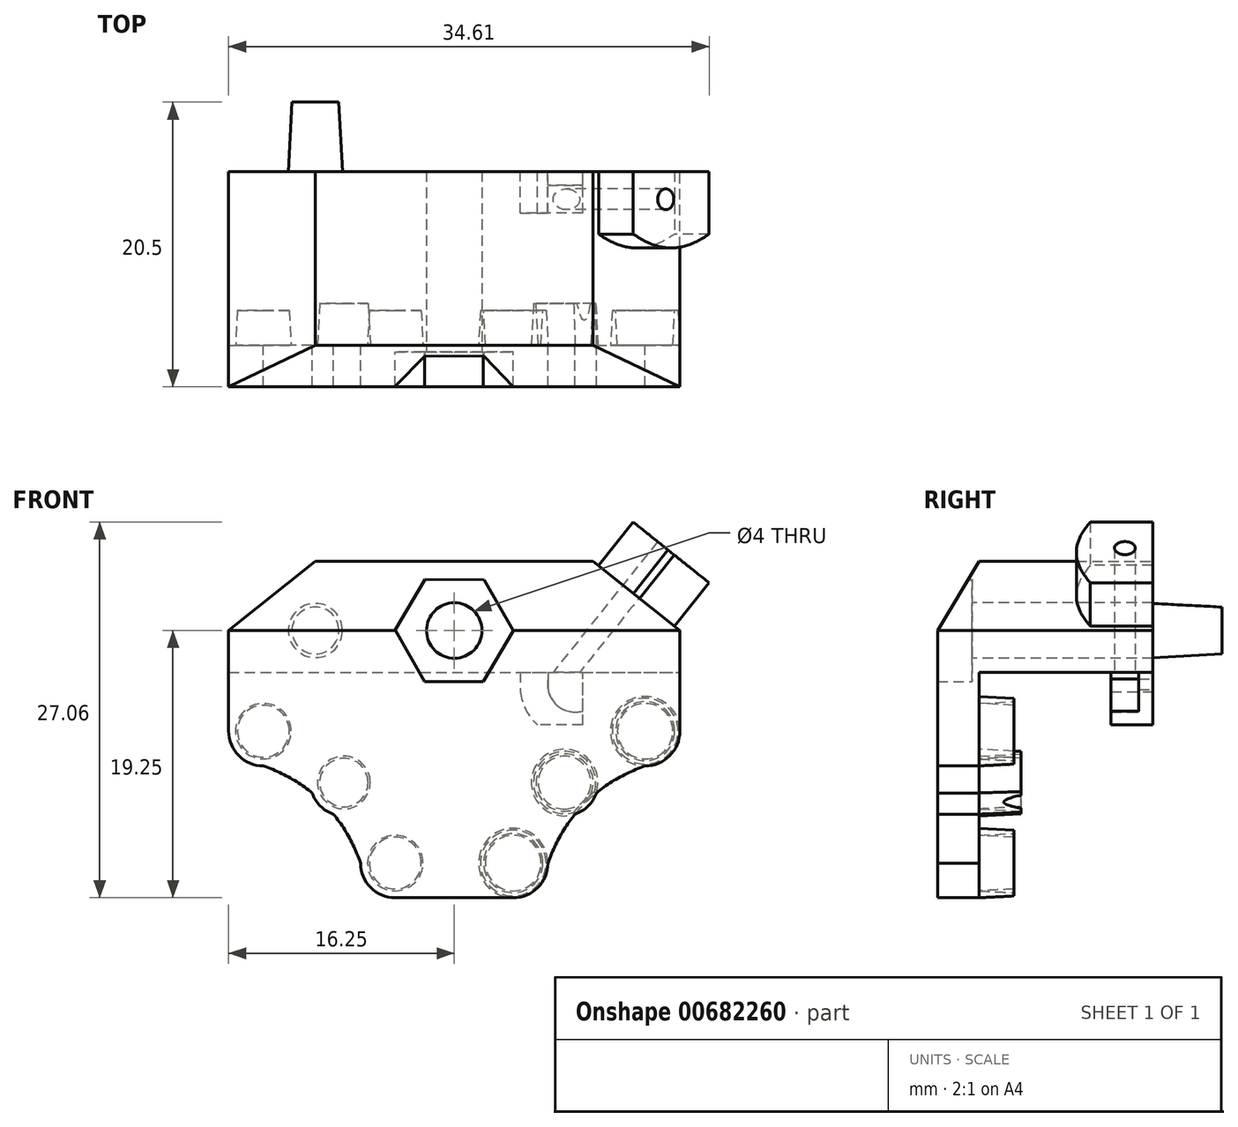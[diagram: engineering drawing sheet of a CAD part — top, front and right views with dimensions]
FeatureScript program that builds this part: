
annotation { "Feature Type Name" : "Feature", "Feature Type Description" : "" }
export const myFeature = defineFeature(function(context is Context, id is Id, definition is map)
    precondition{}
    {
        {
            var Q0;
            Q0=qCreatedBy(makeId("Front.planeOp"),FACE);
            var sketch = newSketch(context, id + "F0", { "sketchPlane" : qUnion([Q0])});
            skLineSegment(sketch, "E0", {"start": v(0, 0) * mm, "end": v(-4.25, 0) * mm});
            skLineSegment(sketch, "E1", {"start": v(0, 0) * mm, "end": v(0, -4.25) * mm});
            skLineSegment(sketch, "E2", {"start": v(0, 0) * mm, "end": v(0, -7.95) * mm});
            skLineSegment(sketch, "E3", {"start": v(0, 0) * mm, "end": v(-7.95, 0) * mm});
            skLineSegment(sketch, "E4", {"start": v(0, 0) * mm, "end": v(0, -13.75) * mm});
            skLineSegment(sketch, "E5", {"start": v(0, 0) * mm, "end": v(-13.75, 0) * mm});
            skCircle(sketch, "E6", {"center": v(-4.25, -13.75) * mm, "radius": 2 * mm});
            skCircle(sketch, "E7", {"center": v(-13.75, -4.25) * mm, "radius": 2 * mm});
            skCircle(sketch, "E8", {"center": v(-7.95, -7.95) * mm, "radius": 1.9 * mm});
            skLineSegment(sketch, "E9", {"start": v(0, 0) * mm, "end": v(0, 3) * mm});
            skCircle(sketch, "E10", {"center": v(0, 3) * mm, "radius": 2 * mm});
            skCircle(sketch, "E11.cCircle", {"center": v(0, 3) * mm, "radius": 4.25 * mm, "construction": true});
            skLineSegment(sketch, "E11.0", {"start": v(2.15, 6.67) * mm, "end": v(4.25, 2.97) * mm});
            skLineSegment(sketch, "E11.1", {"start": v(4.25, 2.97) * mm, "end": v(2.1, -0.7) * mm});
            skLineSegment(sketch, "E11.2", {"start": v(2.1, -0.7) * mm, "end": v(-2.15, -0.67) * mm});
            skLineSegment(sketch, "E11.3", {"start": v(-2.15, -0.67) * mm, "end": v(-4.25, 3.03) * mm});
            skLineSegment(sketch, "E11.4", {"start": v(-4.25, 3.03) * mm, "end": v(-2.1, 6.7) * mm});
            skLineSegment(sketch, "E11.5", {"start": v(-2.1, 6.7) * mm, "end": v(2.15, 6.67) * mm});
            skCircle(sketch, "E12.MirrorC", {"center": v(4.25, -13.75) * mm, "radius": 2 * mm});
            skCircle(sketch, "E13.MirrorC", {"center": v(7.95, -7.95) * mm, "radius": 1.9 * mm});
            skCircle(sketch, "E14.MirrorC", {"center": v(13.75, -4.25) * mm, "radius": 2 * mm});
            skLineSegment(sketch, "E15", {"start": v(0, 0) * mm, "end": v(0, 12) * mm});
            skCircle(sketch, "E16", {"center": v(-13.75, -4.25) * mm, "radius": 2.5 * mm});
            skCircle(sketch, "E17", {"center": v(-7.95, -7.95) * mm, "radius": 2.4 * mm});
            skCircle(sketch, "E18", {"center": v(-4.25, -13.75) * mm, "radius": 2.5 * mm});
            skLineSegment(sketch, "E19", {"start": v(-4.25, -16.25) * mm, "end": v(0, -16.25) * mm});
            skLineSegment(sketch, "E20", {"start": v(-16.25, -4.25) * mm, "end": v(-16.25, 0) * mm});
            skLineSegment(sketch, "E21", {"start": v(-16.25, 0) * mm, "end": v(-16.25, 3) * mm});
            skLineSegment(sketch, "E22", {"start": v(-16.25, 3) * mm, "end": v(-10, 8) * mm});
            skLineSegment(sketch, "E23", {"start": v(-10, 8) * mm, "end": v(0, 8) * mm});
            skLineSegment(sketch, "E24.MirrorCS", {"start": v(10, 8) * mm, "end": v(0, 8) * mm});
            skLineSegment(sketch, "E25.MirrorCS", {"start": v(16.25, 3) * mm, "end": v(10, 8) * mm});
            skLineSegment(sketch, "E26.MirrorCS", {"start": v(16.25, 0) * mm, "end": v(16.25, 3) * mm});
            skLineSegment(sketch, "E27.MirrorCS", {"start": v(16.25, -4.25) * mm, "end": v(16.25, 0) * mm});
            skCircle(sketch, "E28.MirrorC", {"center": v(13.75, -4.25) * mm, "radius": 2.5 * mm});
            skCircle(sketch, "E29.MirrorC", {"center": v(4.25, -13.75) * mm, "radius": 2.5 * mm});
            skLineSegment(sketch, "E30.MirrorCS", {"start": v(4.25, -16.25) * mm, "end": v(0, -16.25) * mm});
            skFitSpline(sketch, "E31", {"points": [v(-6.75, -13.75) * mm, v(-13.75, -6.75) * mm], "startDerivative": vector(-3.6, 10.2) * mm, "endDerivative": vector(-10.2, 3.6) * mm});
            skFitSpline(sketch, "E32.MirrorCS", {"points": [v(6.75, -13.75) * mm, v(13.75, -6.75) * mm], "startDerivative": vector(3.6, 10.2) * mm, "endDerivative": vector(10.2, 3.6) * mm});
            skCircle(sketch, "E33.MirrorC", {"center": v(7.95, -7.95) * mm, "radius": 2.4 * mm});
            skLineSegment(sketch, "E34", {"start": v(-16.25, 0) * mm, "end": v(16.25, 0) * mm});
            skSolve(sketch);
        }
        {
            var Q0;
            {var subQ7=sQuery(id+"F0.wireOp",EDGE,"E11.4");Q0=makeQuery(id+"F0.imprint","IMPRINT",FACE,{"disambiguationData":[TD([[makeQuery(id+"F0.imprint","IMPRINT",EDGE,{"derivedFrom":subQ7}),1.0]])]});}
            var Q1;
            {var subQ4=sQuery(id+"F0.wireOp",EDGE,"E11.0");Q1=makeQuery(id+"F0.imprint","IMPRINT",FACE,{"disambiguationData":[TD([[makeQuery(id+"F0.imprint","IMPRINT",EDGE,{"derivedFrom":subQ4}),1.0]])]});}
            var Q2;
            {var subQ31=sQuery(id+"F0.wireOp",EDGE,"E19");Q2=makeQuery(id+"F0.imprint","IMPRINT",FACE,{"disambiguationData":[TD([[makeQuery(id+"F0.imprint","IMPRINT",EDGE,{"derivedFrom":subQ31}),1.0]])]});}
            var Q3;
            {var subQ0=sQuery(id+"F0.wireOp",EDGE,"E31");var subQ1=sQuery(id+"F0.wireOp",EDGE,"E17");var subQ2=makeQuery(id+"F0.imprint","INTERSECT",VERTEX,{"disambiguationData":[OD(0.0)],"derivedFrom":[subQ1,subQ0]});Q3=makeQuery(id+"F0.imprint","IMPRINT",FACE,{"disambiguationData":[TD([[makeQuery(id+"F0.imprint","IMPRINT",EDGE,{"disambiguationData":[TD([[subQ2,1.0]])],"derivedFrom":subQ1}),1.0]])]});}
            var Q4;
            Q4=makeQuery(id+"F0.imprint","IMPRINT",FACE,{"disambiguationData":[TD([[makeQuery(id+"F0.imprint","IMPRINT",EDGE,{"derivedFrom":sQuery(id+"F0.wireOp",EDGE,"E8")}),-1.0]])]});
            var Q5;
            Q5=makeQuery(id+"F0.imprint","IMPRINT",FACE,{"disambiguationData":[TD([[makeQuery(id+"F0.imprint","IMPRINT",EDGE,{"derivedFrom":sQuery(id+"F0.wireOp",EDGE,"E8")}),1.0]])]});
            var Q6;
            Q6=makeQuery(id+"F0.imprint","IMPRINT",FACE,{"disambiguationData":[TD([[makeQuery(id+"F0.imprint","IMPRINT",EDGE,{"derivedFrom":sQuery(id+"F0.wireOp",EDGE,"E7")}),-1.0]])]});
            var Q7;
            Q7=makeQuery(id+"F0.imprint","IMPRINT",FACE,{"disambiguationData":[TD([[makeQuery(id+"F0.imprint","IMPRINT",EDGE,{"derivedFrom":sQuery(id+"F0.wireOp",EDGE,"E7")}),1.0]])]});
            var Q8;
            Q8=makeQuery(id+"F0.imprint","IMPRINT",FACE,{"disambiguationData":[TD([[makeQuery(id+"F0.imprint","IMPRINT",EDGE,{"derivedFrom":sQuery(id+"F0.wireOp",EDGE,"E6")}),1.0]])]});
            var Q9;
            Q9=makeQuery(id+"F0.imprint","IMPRINT",FACE,{"disambiguationData":[TD([[makeQuery(id+"F0.imprint","IMPRINT",EDGE,{"derivedFrom":sQuery(id+"F0.wireOp",EDGE,"E6")}),-1.0]])]});
            var Q10;
            Q10=makeQuery(id+"F0.imprint","IMPRINT",FACE,{"disambiguationData":[TD([[makeQuery(id+"F0.imprint","IMPRINT",EDGE,{"derivedFrom":sQuery(id+"F0.wireOp",EDGE,"E12.MirrorC")}),-1.0]])]});
            var Q11;
            Q11=makeQuery(id+"F0.imprint","IMPRINT",FACE,{"disambiguationData":[TD([[makeQuery(id+"F0.imprint","IMPRINT",EDGE,{"derivedFrom":sQuery(id+"F0.wireOp",EDGE,"E12.MirrorC")}),1.0]])]});
            var Q12;
            {var subQ0=sQuery(id+"F0.wireOp",EDGE,"E33.MirrorC");var subQ1=sQuery(id+"F0.wireOp",EDGE,"E32.MirrorCS");var subQ2=makeQuery(id+"F0.imprint","INTERSECT",VERTEX,{"disambiguationData":[OD(0.0)],"derivedFrom":[subQ1,subQ0]});Q12=makeQuery(id+"F0.imprint","IMPRINT",FACE,{"disambiguationData":[TD([[makeQuery(id+"F0.imprint","IMPRINT",EDGE,{"disambiguationData":[TD([[subQ2,-1.0]])],"derivedFrom":subQ1}),-1.0]])]});}
            var Q13;
            Q13=makeQuery(id+"F0.imprint","IMPRINT",FACE,{"disambiguationData":[TD([[makeQuery(id+"F0.imprint","IMPRINT",EDGE,{"derivedFrom":sQuery(id+"F0.wireOp",EDGE,"E13.MirrorC")}),1.0]])]});
            var Q14;
            Q14=makeQuery(id+"F0.imprint","IMPRINT",FACE,{"disambiguationData":[TD([[makeQuery(id+"F0.imprint","IMPRINT",EDGE,{"derivedFrom":sQuery(id+"F0.wireOp",EDGE,"E13.MirrorC")}),-1.0]])]});
            var Q15;
            Q15=makeQuery(id+"F0.imprint","IMPRINT",FACE,{"disambiguationData":[TD([[makeQuery(id+"F0.imprint","IMPRINT",EDGE,{"derivedFrom":sQuery(id+"F0.wireOp",EDGE,"E14.MirrorC")}),1.0]])]});
            var Q16;
            Q16=makeQuery(id+"F0.imprint","IMPRINT",FACE,{"disambiguationData":[TD([[makeQuery(id+"F0.imprint","IMPRINT",EDGE,{"derivedFrom":sQuery(id+"F0.wireOp",EDGE,"E14.MirrorC")}),-1.0]])]});
            extrude(context, id + "F1", {"entities" : qUnion([Q0, Q1, Q2, Q3, Q4, Q5, Q6, Q7, Q8, Q9, Q10, Q11, Q12, Q13, Q14, Q15, Q16]), "depth" : 3 * mm, "offsetDistance" : 25 * mm});
        }
        {
            var Q0;
            Q0=makeQuery(id+"F0.imprint","IMPRINT",FACE,{"disambiguationData":[TD([[makeQuery(id+"F0.imprint","IMPRINT",EDGE,{"derivedFrom":sQuery(id+"F0.wireOp",EDGE,"E8")}),1.0]])]});
            var Q1;
            Q1=makeQuery(id+"F0.imprint","IMPRINT",FACE,{"disambiguationData":[TD([[makeQuery(id+"F0.imprint","IMPRINT",EDGE,{"derivedFrom":sQuery(id+"F0.wireOp",EDGE,"E13.MirrorC")}),-1.0]])]});
            extrude(context, id + "F2", {"entities" : qUnion([Q0, Q1]), "operationType" : NewBodyOperationType.ADD, "oppositeDirection" : true, "depth" : 3 * mm, "offsetDistance" : 25 * mm, "hasDraft" : true, "draftAngle" : 3 * degree, "draftPullDirection" : true});
        }
        {
            var Q0;
            {var subQ7=sQuery(id+"F0.wireOp",EDGE,"E11.4");Q0=makeQuery(id+"F0.imprint","IMPRINT",FACE,{"disambiguationData":[TD([[makeQuery(id+"F0.imprint","IMPRINT",EDGE,{"derivedFrom":subQ7}),1.0]])]});}
            var Q1;
            {var subQ4=sQuery(id+"F0.wireOp",EDGE,"E11.0");Q1=makeQuery(id+"F0.imprint","IMPRINT",FACE,{"disambiguationData":[TD([[makeQuery(id+"F0.imprint","IMPRINT",EDGE,{"derivedFrom":subQ4}),1.0]])]});}
            var Q2;
            {var subQ1=sQuery(id+"F0.wireOp",EDGE,"E11.0");Q2=makeQuery(id+"F0.imprint","IMPRINT",FACE,{"disambiguationData":[TD([[makeQuery(id+"F0.imprint","IMPRINT",EDGE,{"derivedFrom":subQ1}),-1.0]])]});}
            var Q3;
            {var subQ0=sQuery(id+"F0.wireOp",EDGE,"E11.4");Q3=makeQuery(id+"F0.imprint","IMPRINT",FACE,{"disambiguationData":[TD([[makeQuery(id+"F0.imprint","IMPRINT",EDGE,{"derivedFrom":subQ0}),-1.0]])]});}
            extrude(context, id + "F3", {"entities" : qUnion([Q0, Q1, Q2, Q3]), "operationType" : NewBodyOperationType.ADD, "oppositeDirection" : true, "depth" : 12.5 * mm, "offsetDistance" : 25 * mm});
        }
        {
            var Q0;
            Q0=makeQuery(id+"F1.opExtrude","CAP_EDGE",EDGE,{"disambiguationData":[OSD([sQuery(id+"F0.wireOp",EDGE,"E23"),sQuery(id+"F0.wireOp",EDGE,"E24.MirrorCS")])],"isStart":false});
            chamfer(context, id + "F4", {"entities" : qUnion([Q0]), "chamferType" : ChamferType.TWO_OFFSETS, "width1" : 3 * mm, "oppositeDirection" : false, "width2" : 5 * mm, "tangentPropagation" : true});
        }
        {
            var Q0;
            Q0=makeQuery(id+"F0.imprint","IMPRINT",FACE,{"disambiguationData":[TD([[makeQuery(id+"F0.imprint","IMPRINT",EDGE,{"derivedFrom":sQuery(id+"F0.wireOp",EDGE,"E14.MirrorC")}),-1.0]])]});
            var Q1;
            Q1=makeQuery(id+"F0.imprint","IMPRINT",FACE,{"disambiguationData":[TD([[makeQuery(id+"F0.imprint","IMPRINT",EDGE,{"derivedFrom":sQuery(id+"F0.wireOp",EDGE,"E12.MirrorC")}),-1.0]])]});
            var Q2;
            Q2=makeQuery(id+"F0.imprint","IMPRINT",FACE,{"disambiguationData":[TD([[makeQuery(id+"F0.imprint","IMPRINT",EDGE,{"derivedFrom":sQuery(id+"F0.wireOp",EDGE,"E6")}),1.0]])]});
            var Q3;
            Q3=makeQuery(id+"F0.imprint","IMPRINT",FACE,{"disambiguationData":[TD([[makeQuery(id+"F0.imprint","IMPRINT",EDGE,{"derivedFrom":sQuery(id+"F0.wireOp",EDGE,"E7")}),1.0]])]});
            extrude(context, id + "F5", {"entities" : qUnion([Q0, Q1, Q2, Q3]), "operationType" : NewBodyOperationType.ADD, "oppositeDirection" : true, "depth" : 2.5 * mm, "offsetDistance" : 25 * mm, "hasDraft" : true, "draftAngle" : 3 * degree, "draftPullDirection" : true});
        }
        {
            var Q0;
            Q0=makeQuery(id+"F3.opExtrude","CAP_FACE",FACE,{"disambiguationData":[OSD([sQuery(id+"F0.wireOp",EDGE,"E10"),sQuery(id+"F0.wireOp",EDGE,"E21"),sQuery(id+"F0.wireOp",EDGE,"E22"),sQuery(id+"F0.wireOp",EDGE,"E23"),sQuery(id+"F0.wireOp",EDGE,"E24.MirrorCS"),sQuery(id+"F0.wireOp",EDGE,"E25.MirrorCS"),sQuery(id+"F0.wireOp",EDGE,"E26.MirrorCS"),sQuery(id+"F0.wireOp",EDGE,"E34")])],"isStart":false});
            var sketch = newSketch(context, id + "F6", { "sketchPlane" : qUnion([Q0])});
            skLineSegment(sketch, "E35", {"start": v(0, 0) * mm, "end": v(0, 3) * mm});
            skLineSegment(sketch, "E36", {"start": v(0, 3) * mm, "end": v(10, 3) * mm});
            skLineSegment(sketch, "E37", {"start": v(0, 3) * mm, "end": v(-10, 3) * mm});
            skCircle(sketch, "E38", {"center": v(-10, 3) * mm, "radius": 2.05 * mm});
            skCircle(sketch, "E39", {"center": v(10, 3) * mm, "radius": 1.95 * mm});
            skSolve(sketch);
        }
        {
            var Q0;
            Q0=makeQuery(id+"F6.imprint","IMPRINT",FACE,{"disambiguationData":[TD([[makeQuery(id+"F6.imprint","IMPRINT",EDGE,{"derivedFrom":sQuery(id+"F6.wireOp",EDGE,"E39")}),1.0]])]});
            extrude(context, id + "F7", {"entities" : qUnion([Q0]), "operationType" : NewBodyOperationType.ADD, "depth" : 5 * mm, "offsetDistance" : 25 * mm, "hasDraft" : true, "draftAngle" : 3 * degree, "draftPullDirection" : true});
        }
        {
            var Q0;
            {var subQ3=sQuery(id+"F0.wireOp",EDGE,"E11.2");var subQ5=sQuery(id+"F0.wireOp",EDGE,"E11.3");var subQ6=makeQuery(id+"F0.imprint","INTERSECT",VERTEX,{"derivedFrom":[subQ3,subQ5]});Q0=makeQuery(id+"F0.imprint","IMPRINT",FACE,{"disambiguationData":[TD([[makeQuery(id+"F0.imprint","IMPRINT",EDGE,{"disambiguationData":[TD([[subQ6,1.0]])],"derivedFrom":subQ3}),-1.0]])]});}
            var Q1;
            {var subQ3=sQuery(id+"F0.wireOp",EDGE,"E11.2");var subQ5=sQuery(id+"F0.wireOp",EDGE,"E11.1");var subQ6=makeQuery(id+"F0.imprint","INTERSECT",VERTEX,{"derivedFrom":[subQ5,subQ3]});Q1=makeQuery(id+"F0.imprint","IMPRINT",FACE,{"disambiguationData":[TD([[makeQuery(id+"F0.imprint","IMPRINT",EDGE,{"disambiguationData":[TD([[subQ6,1.0]])],"derivedFrom":subQ5}),-1.0]])]});}
            var Q2;
            {var subQ1=sQuery(id+"F0.wireOp",EDGE,"E11.0");Q2=makeQuery(id+"F0.imprint","IMPRINT",FACE,{"disambiguationData":[TD([[makeQuery(id+"F0.imprint","IMPRINT",EDGE,{"derivedFrom":subQ1}),-1.0]])]});}
            var Q3;
            {var subQ0=sQuery(id+"F0.wireOp",EDGE,"E11.4");Q3=makeQuery(id+"F0.imprint","IMPRINT",FACE,{"disambiguationData":[TD([[makeQuery(id+"F0.imprint","IMPRINT",EDGE,{"derivedFrom":subQ0}),-1.0]])]});}
            extrude(context, id + "F8", {"entities" : qUnion([Q0, Q1, Q2, Q3]), "operationType" : NewBodyOperationType.ADD, "depth" : 0.5 * mm, "offsetDistance" : 25 * mm});
        }
        {
            var Q0;
            {var subQ0=sQuery(id+"F0.wireOp",EDGE,"E25.MirrorCS");Q0=makeQuery(id+"F3.boolean.opBoolean","MERGE",FACE,{"derivedFrom":[makeQuery(id+"F1.opExtrude","SWEPT_FACE",FACE,{"disambiguationData":[OSD([subQ0])]}),makeQuery(id+"F3.opExtrude","SWEPT_FACE",FACE,{"disambiguationData":[OSD([subQ0])]})]});}
            var sketch = newSketch(context, id + "F9", { "sketchPlane" : qUnion([Q0])});
            skLineSegment(sketch, "E40.bottom", {"start": v(3.31, 12.5) * mm, "end": v(10.31, 12.5) * mm});
            skLineSegment(sketch, "E40.top", {"start": v(3.31, 7) * mm, "end": v(10.31, 7) * mm});
            skLineSegment(sketch, "E40.left", {"start": v(3.31, 12.5) * mm, "end": v(3.31, 7) * mm});
            skLineSegment(sketch, "E40.right", {"start": v(10.31, 12.5) * mm, "end": v(10.31, 7) * mm});
            skLineSegment(sketch, "E41", {"start": v(3.31, 12.5) * mm, "end": v(3.31, 8) * mm});
            skLineSegment(sketch, "E42", {"start": v(10.31, 12.5) * mm, "end": v(10.31, 8) * mm});
            skFitSpline(sketch, "E43", {"points": [v(3.31, 8) * mm, v(10.31, 8) * mm], "startDerivative": vector(7.5, -4.03) * mm, "endDerivative": vector(7.5, 4.03) * mm});
            skCircle(sketch, "E44", {"center": v(6.31, 10.5) * mm, "radius": 0.75 * mm});
            skSolve(sketch);
        }
        {
            var Q0;
            Q0=makeQuery(id+"F9.imprint","IMPRINT",FACE,{"disambiguationData":[TD([[makeQuery(id+"F9.imprint","IMPRINT",EDGE,{"derivedFrom":sQuery(id+"F9.wireOp",EDGE,"E40.bottom")}),1.0]])]});
            extrude(context, id + "F10", {"entities" : qUnion([Q0]), "operationType" : NewBodyOperationType.ADD, "depth" : 4 * mm, "offsetDistance" : 25 * mm});
        }
        {
            var Q0;
            {var subQ0=sQuery(id+"F0.wireOp",EDGE,"E25.MirrorCS");Q0=makeQuery(id+"F10.boolean.opBoolean","SPLIT",FACE,{"disambiguationData":[TD([makeQuery(id+"F10.opExtrude","SWEPT_FACE",FACE,{"disambiguationData":[OSD([sQuery(id+"F9.wireOp",EDGE,"E44")])]})])],"derivedFrom":makeQuery(id+"F3.boolean.opBoolean","MERGE",FACE,{"derivedFrom":[makeQuery(id+"F1.opExtrude","SWEPT_FACE",FACE,{"disambiguationData":[OSD([subQ0])]}),makeQuery(id+"F3.opExtrude","SWEPT_FACE",FACE,{"disambiguationData":[OSD([subQ0])]})]})});}
            extrude(context, id + "F11", {"entities" : qUnion([Q0]), "operationType" : NewBodyOperationType.REMOVE, "oppositeDirection" : true, "depth" : 8.2 * mm, "offsetDistance" : 25 * mm});
        }
        {
            var Q0;
            Q0=makeQuery(id+"F6.imprint","IMPRINT",FACE,{"disambiguationData":[TD([[makeQuery(id+"F6.imprint","IMPRINT",EDGE,{"derivedFrom":sQuery(id+"F6.wireOp",EDGE,"E38")}),-1.0]])]});
            var sketch = newSketch(context, id + "F12", { "sketchPlane" : qUnion([Q0])});
            skLineSegment(sketch, "E45.bottom", {"start": v(-6.75, 0) * mm, "end": v(-4.75, 0) * mm});
            skLineSegment(sketch, "E45.top", {"start": v(-6.75, -3.8) * mm, "end": v(-4.75, -3.8) * mm});
            skLineSegment(sketch, "E45.left", {"start": v(-6.75, 0) * mm, "end": v(-6.75, -3.8) * mm});
            skLineSegment(sketch, "E45.right", {"start": v(-4.75, 0) * mm, "end": v(-4.75, -3.8) * mm});
            skLineSegment(sketch, "E46.bottom", {"start": v(-6.75, -3.8) * mm, "end": v(-9.25, -3.8) * mm});
            skLineSegment(sketch, "E46.top", {"start": v(-6.75, 0) * mm, "end": v(-9.25, 0) * mm});
            skLineSegment(sketch, "E46.left", {"start": v(-6.75, -3.8) * mm, "end": v(-6.75, 0) * mm});
            skLineSegment(sketch, "E46.right", {"start": v(-9.25, -3.8) * mm, "end": v(-9.25, 0) * mm});
            skArc(sketch, "E47", {"start": v(-9.25, -2.8) * mm, "mid": v(-7.36, -2.34) * mm, "end": v(-6.75, -0.5) * mm});
            skArc(sketch, "E48.0", {"start": v(-9.79, -4.73) * mm, "mid": v(-6.09, -3.9) * mm, "end": v(-4.75, -0.34) * mm});
            skSolve(sketch);
        }
        {
            var Q0;
            {var subQ1=sQuery(id+"F12.wireOp",EDGE,"E46.top");Q0=makeQuery(id+"F12.imprint","IMPRINT",FACE,{"disambiguationData":[TD([[makeQuery(id+"F12.imprint","IMPRINT",EDGE,{"derivedFrom":subQ1}),1.0]])]});}
            extrude(context, id + "F13", {"entities" : qUnion([Q0]), "operationType" : NewBodyOperationType.ADD, "oppositeDirection" : true, "depth" : 1 * mm, "offsetDistance" : 25 * mm});
        }
        {
            var Q0;
            {var subQ6=sQuery(id+"F12.wireOp",EDGE,"E45.bottom");Q0=makeQuery(id+"F12.imprint","IMPRINT",FACE,{"disambiguationData":[TD([[makeQuery(id+"F12.imprint","IMPRINT",EDGE,{"derivedFrom":subQ6}),1.0]])]});}
            var Q1;
            {var subQ0=sQuery(id+"F12.wireOp",EDGE,"E46.bottom");Q1=makeQuery(id+"F12.imprint","IMPRINT",FACE,{"disambiguationData":[TD([[makeQuery(id+"F12.imprint","IMPRINT",EDGE,{"derivedFrom":subQ0}),-1.0]])]});}
            extrude(context, id + "F14", {"entities" : qUnion([Q0, Q1]), "operationType" : NewBodyOperationType.ADD, "oppositeDirection" : true, "depth" : 3 * mm, "offsetDistance" : 25 * mm});
        }
    });
